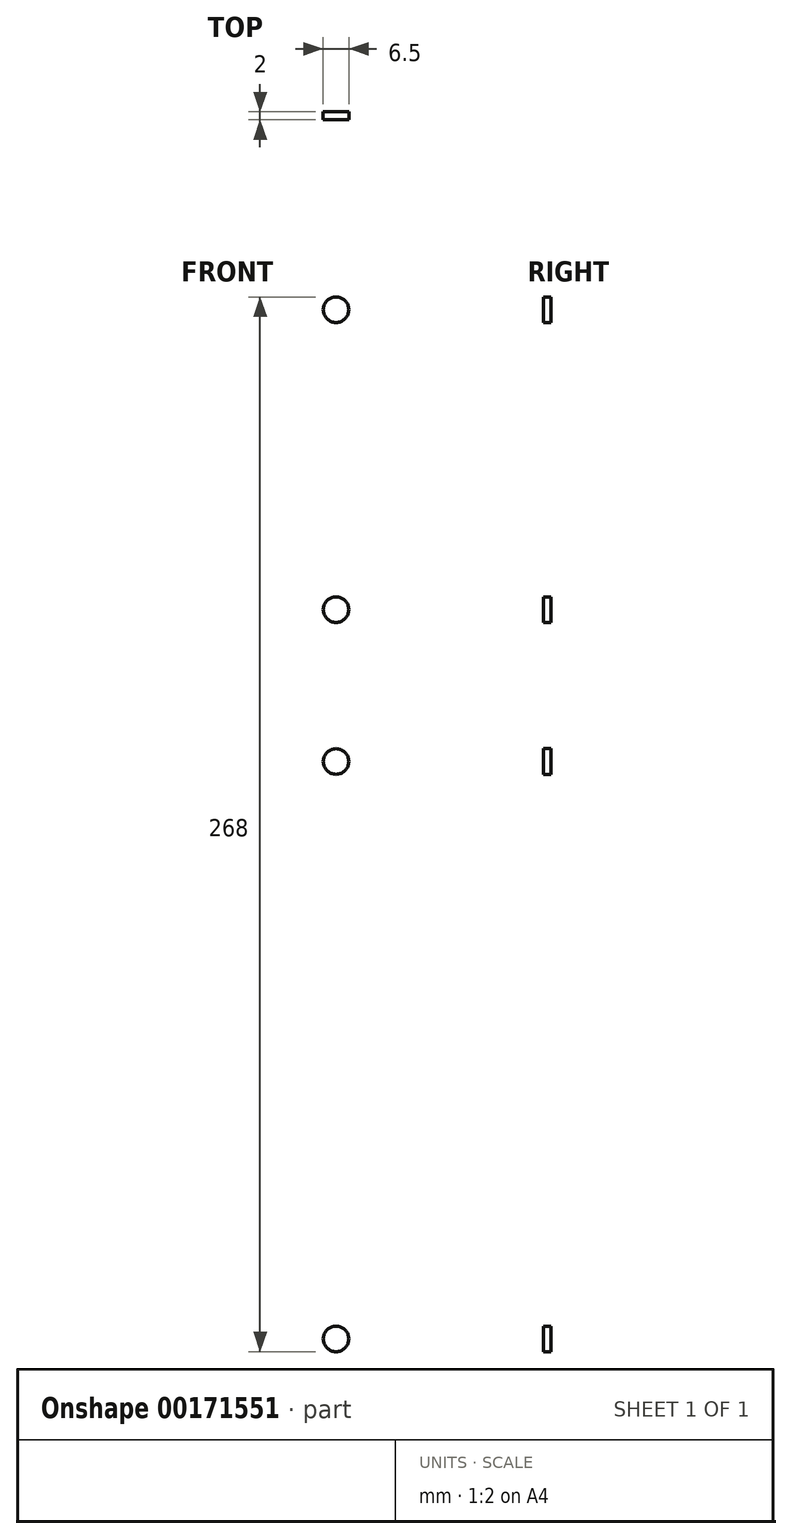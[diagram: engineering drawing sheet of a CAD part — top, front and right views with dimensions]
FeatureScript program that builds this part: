
annotation { "Feature Type Name" : "Feature", "Feature Type Description" : "" }
export const myFeature = defineFeature(function(context is Context, id is Id, definition is map)
    precondition{}
    {
        {
            var Q0;
            Q0=qCreatedBy(makeId("Front.planeOp"),FACE);
            var sketch = newSketch(context, id + "F0", { "sketchPlane" : qUnion([Q0])});
            skLineSegment(sketch, "E0.bottom", {"start": v(178.05, -104.5) * mm, "end": v(154.55, -104.5) * mm});
            skLineSegment(sketch, "E0.top", {"start": v(178.05, -125.5) * mm, "end": v(154.55, -125.5) * mm});
            skLineSegment(sketch, "E0.left", {"start": v(180.55, -107) * mm, "end": v(180.55, -123) * mm});
            skLineSegment(sketch, "E0.right", {"start": v(152.05, -107) * mm, "end": v(152.05, -123) * mm});
            skPoint(sketch, "E0.middle", {"position": v(166.3, -115) * mm});
            skCircle(sketch, "E1", {"center": v(146.3, -115) * mm, "radius": 2.25 * mm});
            skPoint(sketch, "E1.centerSnap0", {"position": v(152.05, -115) * mm});
            skCircle(sketch, "E2", {"center": v(186.3, -115) * mm, "radius": 2.25 * mm});
            skPoint(sketch, "E3.visualSharp", {"position": v(152.05, -104.5) * mm});
            skArc(sketch, "E3.filletArc", {"start": v(154.55, -104.5) * mm, "mid": v(152.78, -105.23) * mm, "end": v(152.05, -107) * mm});
            skPoint(sketch, "E4.visualSharp", {"position": v(180.55, -104.5) * mm});
            skArc(sketch, "E4.filletArc", {"start": v(180.55, -107) * mm, "mid": v(179.82, -105.23) * mm, "end": v(178.05, -104.5) * mm});
            skPoint(sketch, "E5.visualSharp", {"position": v(180.55, -125.5) * mm});
            skArc(sketch, "E5.filletArc", {"start": v(178.05, -125.5) * mm, "mid": v(179.82, -124.77) * mm, "end": v(180.55, -123) * mm});
            skPoint(sketch, "E6.visualSharp", {"position": v(152.05, -125.5) * mm});
            skArc(sketch, "E6.filletArc", {"start": v(152.05, -123) * mm, "mid": v(152.78, -124.77) * mm, "end": v(154.55, -125.5) * mm});
            skLineSegment(sketch, "E7.bottom", {"start": v(190.3, -103.5) * mm, "end": v(142.3, -103.5) * mm, "construction": true});
            skLineSegment(sketch, "E7.top", {"start": v(190.3, -126.5) * mm, "end": v(142.3, -126.5) * mm, "construction": true});
            skLineSegment(sketch, "E7.left", {"start": v(190.3, -103.5) * mm, "end": v(190.3, -126.5) * mm, "construction": true});
            skLineSegment(sketch, "E7.right", {"start": v(142.3, -103.5) * mm, "end": v(142.3, -126.5) * mm, "construction": true});
            skArc(sketch, "E8", {"start": v(123.4, -109.35) * mm, "mid": v(126.3, -121.35) * mm, "end": v(129.2, -109.35) * mm});
            skLineSegment(sketch, "E9", {"start": v(123.4, -109.35) * mm, "end": v(129.2, -109.35) * mm});
            skLineSegment(sketch, "E10.bottom", {"start": v(226.3, 188) * mm, "end": v(-226.3, 188) * mm});
            skLineSegment(sketch, "E10.top", {"start": v(226.3, -188) * mm, "end": v(-226.3, -188) * mm});
            skLineSegment(sketch, "E10.left", {"start": v(259.3, 155) * mm, "end": v(259.3, -155) * mm});
            skLineSegment(sketch, "E10.right", {"start": v(-259.3, 155) * mm, "end": v(-259.3, -155) * mm});
            skPoint(sketch, "E10.middle", {"position": v(0, 0) * mm});
            skLineSegment(sketch, "E11.MirrorCS", {"start": v(-226.3, -188) * mm, "end": v(-226.3, -155) * mm});
            skLineSegment(sketch, "E12.MirrorCS", {"start": v(226.3, -188) * mm, "end": v(226.3, -155) * mm});
            skLineSegment(sketch, "E13.MirrorCS", {"start": v(259.3, -155) * mm, "end": v(226.3, -155) * mm});
            skLineSegment(sketch, "E14", {"start": v(226.3, 188) * mm, "end": v(226.3, 155) * mm});
            skLineSegment(sketch, "E15", {"start": v(226.3, 155) * mm, "end": v(259.3, 155) * mm});
            skPoint(sketch, "E16.MirrorCS.start.orphan", {"position": v(-226.3, -188) * mm});
            skPoint(sketch, "E17.MirrorCS.start.orphan", {"position": v(-259.3, -155) * mm});
            skLineSegment(sketch, "E18", {"start": v(-259.3, -155) * mm, "end": v(-226.3, -155) * mm});
            skLineSegment(sketch, "E19", {"start": v(-259.3, 155) * mm, "end": v(-226.3, 155) * mm});
            skLineSegment(sketch, "E20", {"start": v(-226.3, 188) * mm, "end": v(-226.3, 155) * mm});
            skSolve(sketch);
        }
        {
            var Q0;
            Q0=makeQuery(id+"F0.imprint","IMPRINT",FACE,{"disambiguationData":[TD([[makeQuery(id+"F0.imprint","IMPRINT",EDGE,{"derivedFrom":sQuery(id+"F0.wireOp",EDGE,"m8v4xXy7-gdJa-Q9wc-X33C-IR2vLZY9jmVz.bottom")}),1.0]])]});
            var Q1;
            Q1=makeQuery(id+"F0.imprint","IMPRINT",FACE,{"disambiguationData":[TD([[makeQuery(id+"F0.imprint","IMPRINT",EDGE,{"derivedFrom":sQuery(id+"F0.wireOp",EDGE,"m8v4xXy7-gdJa-Q9wc-X33C-IR2vLZY9jmVz.right")}),-1.0]])]});
            var Q2;
            Q2=makeQuery(id+"F0.imprint","IMPRINT",FACE,{"disambiguationData":[TD([[makeQuery(id+"F0.imprint","IMPRINT",EDGE,{"derivedFrom":sQuery(id+"F0.wireOp",EDGE,"m8v4xXy7-gdJa-Q9wc-X33C-IR2vLZY9jmVz.bottom")}),-1.0]])]});
            var Q3;
            Q3=makeQuery(id+"F0.imprint","IMPRINT",FACE,{"disambiguationData":[TD([[makeQuery(id+"F0.imprint","IMPRINT",EDGE,{"derivedFrom":sQuery(id+"F0.wireOp",EDGE,"m8v4xXy7-gdJa-Q9wc-X33C-IR2vLZY9jmVz.top")}),1.0]])]});
            var Q4;
            Q4=makeQuery(id+"F0.imprint","IMPRINT",FACE,{"disambiguationData":[TD([[makeQuery(id+"F0.imprint","IMPRINT",EDGE,{"derivedFrom":sQuery(id+"F0.wireOp",EDGE,"m8v4xXy7-gdJa-Q9wc-X33C-IR2vLZY9jmVz.left")}),1.0]])]});
            var Q5;
            Q5=makeQuery(id+"F0.imprint","IMPRINT",FACE,{"disambiguationData":[TD([[makeQuery(id+"F0.imprint","IMPRINT",EDGE,{"derivedFrom":sQuery(id+"F0.wireOp",EDGE,"E0.bottom")}),-1.0]])]});
            extrude(context, id + "F1", {"entities" : qUnion([Q0, Q1, Q2, Q3, Q4, Q5]), "endBound" : BoundingType.SYMMETRIC, "depth" : 2 * mm});
        }
        {
            var Q0;
            Q0=makeQuery(id+"F1.opExtrude","SWEPT_EDGE",EDGE,{"disambiguationData":[OSD([sQuery(id+"F0.wireOp",EDGE,"E10.bottom"),sQuery(id+"F0.wireOp",EDGE,"E14")])]});
            var Q1;
            Q1=makeQuery(id+"F1.opExtrude","SWEPT_EDGE",EDGE,{"disambiguationData":[OSD([sQuery(id+"F0.wireOp",EDGE,"E10.left"),sQuery(id+"F0.wireOp",EDGE,"E15")])]});
            var Q2;
            Q2=makeQuery(id+"F1.opExtrude","SWEPT_EDGE",EDGE,{"disambiguationData":[OSD([sQuery(id+"F0.wireOp",EDGE,"E10.left"),sQuery(id+"F0.wireOp",EDGE,"E13.MirrorCS")])]});
            var Q3;
            Q3=makeQuery(id+"F1.opExtrude","SWEPT_EDGE",EDGE,{"disambiguationData":[OSD([sQuery(id+"F0.wireOp",EDGE,"E10.top"),sQuery(id+"F0.wireOp",EDGE,"E12.MirrorCS")])]});
            var Q4;
            Q4=makeQuery(id+"F1.opExtrude","SWEPT_EDGE",EDGE,{"disambiguationData":[OSD([sQuery(id+"F0.wireOp",EDGE,"E10.bottom"),sQuery(id+"F0.wireOp",EDGE,"E20")])]});
            var Q5;
            Q5=makeQuery(id+"F1.opExtrude","SWEPT_EDGE",EDGE,{"disambiguationData":[OSD([sQuery(id+"F0.wireOp",EDGE,"E10.right"),sQuery(id+"F0.wireOp",EDGE,"E19")])]});
            var Q6;
            Q6=makeQuery(id+"F1.opExtrude","SWEPT_EDGE",EDGE,{"disambiguationData":[OSD([sQuery(id+"F0.wireOp",EDGE,"E10.right"),sQuery(id+"F0.wireOp",EDGE,"E18")])]});
            var Q7;
            Q7=makeQuery(id+"F1.opExtrude","SWEPT_EDGE",EDGE,{"disambiguationData":[OSD([sQuery(id+"F0.wireOp",EDGE,"E10.top"),sQuery(id+"F0.wireOp",EDGE,"E11.MirrorCS")])]});
            chamfer(context, id + "F2", {"entities" : qUnion([Q0, Q1, Q2, Q3, Q4, Q5, Q6, Q7]), "width" : 7.5 * mm, "tangentPropagation" : true});
        }
        {
            var Q0;
            Q0=makeQuery(id+"F1.opExtrude","CAP_FACE",FACE,{"disambiguationData":[OSD([sQuery(id+"F0.wireOp",EDGE,"E0.bottom"),sQuery(id+"F0.wireOp",EDGE,"E0.top"),sQuery(id+"F0.wireOp",EDGE,"E0.left"),sQuery(id+"F0.wireOp",EDGE,"E0.right"),sQuery(id+"F0.wireOp",EDGE,"E1"),sQuery(id+"F0.wireOp",EDGE,"E2"),sQuery(id+"F0.wireOp",EDGE,"E3.filletArc"),sQuery(id+"F0.wireOp",EDGE,"E4.filletArc"),sQuery(id+"F0.wireOp",EDGE,"E5.filletArc"),sQuery(id+"F0.wireOp",EDGE,"E6.filletArc"),sQuery(id+"F0.wireOp",EDGE,"E8"),sQuery(id+"F0.wireOp",EDGE,"E9"),sQuery(id+"F0.wireOp",EDGE,"L87DZw3D-RKXx-xFcY-jME4-4X5ltL9unzp5.bottom"),sQuery(id+"F0.wireOp",EDGE,"L87DZw3D-RKXx-xFcY-jME4-4X5ltL9unzp5.top"),sQuery(id+"F0.wireOp",EDGE,"L87DZw3D-RKXx-xFcY-jME4-4X5ltL9unzp5.right"),sQuery(id+"F0.wireOp",EDGE,"c8b3b5BV-40K6-DEiQ-IxRp-azOoG3nQCedk.bottom"),sQuery(id+"F0.wireOp",EDGE,"c8b3b5BV-40K6-DEiQ-IxRp-azOoG3nQCedk.top"),sQuery(id+"F0.wireOp",EDGE,"c8b3b5BV-40K6-DEiQ-IxRp-azOoG3nQCedk.right"),sQuery(id+"F0.wireOp",EDGE,"Hnd7Hc7O-F67r-vpp7-kY4p-aV01EXDvk9To.top"),sQuery(id+"F0.wireOp",EDGE,"Hnd7Hc7O-F67r-vpp7-kY4p-aV01EXDvk9To.left"),sQuery(id+"F0.wireOp",EDGE,"Hnd7Hc7O-F67r-vpp7-kY4p-aV01EXDvk9To.right"),sQuery(id+"F0.wireOp",EDGE,"KavZTf65-RkY4-wPDH-55du-rL0O8hMvyGJR.top"),sQuery(id+"F0.wireOp",EDGE,"KavZTf65-RkY4-wPDH-55du-rL0O8hMvyGJR.left"),sQuery(id+"F0.wireOp",EDGE,"KavZTf65-RkY4-wPDH-55du-rL0O8hMvyGJR.right")])],"isStart":false});
            var sketch = newSketch(context, id + "F3", { "sketchPlane" : qUnion([Q0])});
            skLineSegment(sketch, "E21.bottom", {"start": v(-224.05, 157.25) * mm, "end": v(-228.55, 157.25) * mm});
            skLineSegment(sketch, "E21.top", {"start": v(-224.05, 152.75) * mm, "end": v(-228.55, 152.75) * mm});
            skLineSegment(sketch, "E21.left", {"start": v(-224.05, 157.25) * mm, "end": v(-224.05, 152.75) * mm});
            skLineSegment(sketch, "E21.right", {"start": v(-228.55, 157.25) * mm, "end": v(-228.55, 152.75) * mm});
            skPoint(sketch, "E21.middle", {"position": v(-226.3, 155) * mm});
            skPoint(sketch, "E22.MirrorP", {"position": v(226.3, 155) * mm});
            skLineSegment(sketch, "E23.MirrorCS", {"start": v(228.55, 157.25) * mm, "end": v(228.55, 152.75) * mm});
            skLineSegment(sketch, "E24.MirrorCS", {"start": v(224.05, 157.25) * mm, "end": v(228.55, 157.25) * mm});
            skLineSegment(sketch, "E25.MirrorCS", {"start": v(224.05, 157.25) * mm, "end": v(224.05, 152.75) * mm});
            skLineSegment(sketch, "E26.MirrorCS", {"start": v(224.05, 152.75) * mm, "end": v(228.55, 152.75) * mm});
            skLineSegment(sketch, "E27.MirrorCS", {"start": v(-224.05, -157.25) * mm, "end": v(-224.05, -152.75) * mm});
            skLineSegment(sketch, "E28.MirrorCS", {"start": v(-224.05, -152.75) * mm, "end": v(-228.55, -152.75) * mm});
            skLineSegment(sketch, "E29.MirrorCS", {"start": v(-228.55, -157.25) * mm, "end": v(-228.55, -152.75) * mm});
            skLineSegment(sketch, "E30.MirrorCS", {"start": v(-224.05, -157.25) * mm, "end": v(-228.55, -157.25) * mm});
            skLineSegment(sketch, "E31.MirrorCS", {"start": v(224.05, -157.25) * mm, "end": v(224.05, -152.75) * mm});
            skLineSegment(sketch, "E32.MirrorCS", {"start": v(224.05, -152.75) * mm, "end": v(228.55, -152.75) * mm});
            skLineSegment(sketch, "E33.MirrorCS", {"start": v(224.05, -157.25) * mm, "end": v(228.55, -157.25) * mm});
            skLineSegment(sketch, "E34.MirrorCS", {"start": v(228.55, -157.25) * mm, "end": v(228.55, -152.75) * mm});
            skPoint(sketch, "E35.MirrorP", {"position": v(-226.3, -155) * mm});
            skPoint(sketch, "E36.MirrorP", {"position": v(226.3, -155) * mm});
            skCircle(sketch, "E37", {"center": v(-236.6, -112.4) * mm, "radius": 3.25 * mm});
            skCircle(sketch, "E38", {"center": v(-236.6, 34.3) * mm, "radius": 3.25 * mm});
            skCircle(sketch, "E39", {"center": v(-236.6, 149.1) * mm, "radius": 3.25 * mm});
            skCircle(sketch, "E40", {"center": v(-236.6, 72.9) * mm, "radius": 3.25 * mm});
            skCircle(sketch, "E41.MirrorC", {"center": v(236.6, -112.4) * mm, "radius": 3.25 * mm});
            skCircle(sketch, "E42.MirrorC", {"center": v(236.6, 149.1) * mm, "radius": 3.25 * mm});
            skCircle(sketch, "E43.MirrorC", {"center": v(236.6, 72.9) * mm, "radius": 3.25 * mm});
            skCircle(sketch, "E44.MirrorC", {"center": v(236.6, 34.3) * mm, "radius": 3.25 * mm});
            skSolve(sketch);
        }
        {
            var Q0;
            {var subQ2=sQuery(id+"F3.wireOp",EDGE,"E27.MirrorCS");Q0=makeQuery(id+"F3.imprint","IMPRINT",FACE,{"disambiguationData":[TD([[makeQuery(id+"F3.imprint","IMPRINT",EDGE,{"derivedFrom":subQ2}),1.0]])]});}
            var Q1;
            {var subQ1=sQuery(id+"F3.wireOp",EDGE,"E31.MirrorCS");Q1=makeQuery(id+"F3.imprint","IMPRINT",FACE,{"disambiguationData":[TD([[makeQuery(id+"F3.imprint","IMPRINT",EDGE,{"derivedFrom":subQ1}),-1.0]])]});}
            var Q2;
            Q2=makeQuery(id+"F3.imprint","IMPRINT",FACE,{"disambiguationData":[TD([[makeQuery(id+"F3.imprint","IMPRINT",EDGE,{"derivedFrom":sQuery(id+"F3.wireOp",EDGE,"E39")}),1.0]])]});
            var Q3;
            Q3=makeQuery(id+"F3.imprint","IMPRINT",FACE,{"disambiguationData":[TD([[makeQuery(id+"F3.imprint","IMPRINT",EDGE,{"derivedFrom":sQuery(id+"F3.wireOp",EDGE,"E40")}),1.0]])]});
            var Q4;
            Q4=makeQuery(id+"F3.imprint","IMPRINT",FACE,{"disambiguationData":[TD([[makeQuery(id+"F3.imprint","IMPRINT",EDGE,{"derivedFrom":sQuery(id+"F3.wireOp",EDGE,"E38")}),1.0]])]});
            var Q5;
            Q5=makeQuery(id+"F3.imprint","IMPRINT",FACE,{"disambiguationData":[TD([[makeQuery(id+"F3.imprint","IMPRINT",EDGE,{"derivedFrom":sQuery(id+"F3.wireOp",EDGE,"E37")}),1.0]])]});
            var Q6;
            Q6=makeQuery(id+"F3.imprint","IMPRINT",FACE,{"disambiguationData":[TD([[makeQuery(id+"F3.imprint","IMPRINT",EDGE,{"derivedFrom":sQuery(id+"F3.wireOp",EDGE,"E41.MirrorC")}),-1.0]])]});
            var Q7;
            Q7=makeQuery(id+"F3.imprint","IMPRINT",FACE,{"disambiguationData":[TD([[makeQuery(id+"F3.imprint","IMPRINT",EDGE,{"derivedFrom":sQuery(id+"F3.wireOp",EDGE,"E44.MirrorC")}),-1.0]])]});
            var Q8;
            Q8=makeQuery(id+"F3.imprint","IMPRINT",FACE,{"disambiguationData":[TD([[makeQuery(id+"F3.imprint","IMPRINT",EDGE,{"derivedFrom":sQuery(id+"F3.wireOp",EDGE,"E43.MirrorC")}),-1.0]])]});
            var Q9;
            Q9=makeQuery(id+"F3.imprint","IMPRINT",FACE,{"disambiguationData":[TD([[makeQuery(id+"F3.imprint","IMPRINT",EDGE,{"derivedFrom":sQuery(id+"F3.wireOp",EDGE,"E42.MirrorC")}),-1.0]])]});
            var Q10;
            {var subQ1=sQuery(id+"F3.wireOp",EDGE,"E25.MirrorCS");Q10=makeQuery(id+"F3.imprint","IMPRINT",FACE,{"disambiguationData":[TD([[makeQuery(id+"F3.imprint","IMPRINT",EDGE,{"derivedFrom":subQ1}),1.0]])]});}
            var Q11;
            {var subQ2=sQuery(id+"F3.wireOp",EDGE,"E21.left");Q11=makeQuery(id+"F3.imprint","IMPRINT",FACE,{"disambiguationData":[TD([[makeQuery(id+"F3.imprint","IMPRINT",EDGE,{"derivedFrom":subQ2}),-1.0]])]});}
            extrude(context, id + "F4", {"entities" : qUnion([Q0, Q1, Q2, Q3, Q4, Q5, Q6, Q7, Q8, Q9, Q10, Q11]), "operationType" : NewBodyOperationType.REMOVE, "endBound" : BoundingType.UP_TO_NEXT, "oppositeDirection" : true, "depth" : 25 * mm});
        }
    });
